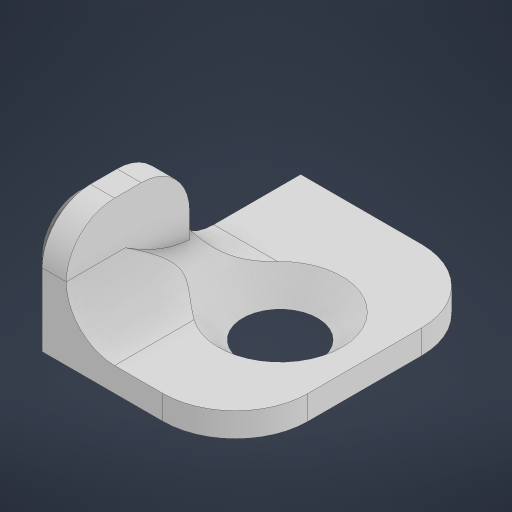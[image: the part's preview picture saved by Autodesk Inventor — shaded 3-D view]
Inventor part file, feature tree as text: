
AUTODESK INVENTOR PART (.ipt)
format: ipt  version: 2024 (Build 280153000, 153)  size: 259,072 bytes
history: native  units: in
note: dims shown in document units (in); Inventor stores cm internally (conversion verified against a paired STEP export)
features: sketch x4, extrude x3, fillet x2, hole x1, chamfer x1
ambient origin geometry x8: Origin, YZ Plane, XZ Plane, XY Plane, X Axis, Y Axis, Z Axis, Center Point
bodies: Solid1 (feature_tree)
feature tree (11):
  extrude  "Extrusion1"  Depth=0.1969in
  hole  "Hole1"  [1 undecoded]
  fillet  "Fillet1"  Radius=0.0394in
  chamfer  "Chamfer2"  Distance=0.1181in
  extrude  "Extrusion5"  Depth=0.0787in TaperAngle=45.0deg
  extrude  "Extrusion6"  Depth=0.0787in
  fillet  "Fillet5"  Radius=0.1004in
  sketch  "Sketch1"  dims[d0=0.315in d1=0.1969in]
  sketch  "Sketch3"  dims[d2=0.0394in d3=0.4213in d4=0.0in d8=0.0394in]
  sketch  "Sketch6"  dims[d11=0.1378in]
  sketch  "Sketch7"  dims[d12=0.2106in d13=0.122in d14=0.2362in d15=0.1575in d16=0.0787in d17=90.0deg d18=0.315in d19=0.8108in d21=0.1181in d36=0.0394in d37=0.2756in d38=45.0deg d39=0.1004in d40=0.1004in d41=0.122in d42=0.0394in d43=0.0in d44=0.2205in d45=0.0394in d46=0.0in d47=0.0787in d22=0.0344in d23=0.0197in d24=0.0344in]
note: 1 required parameter value undecoded (feature->parameter linkage not recoverable at this tier; creation-order binding heuristic only, values carry confidence <= 0.55)
